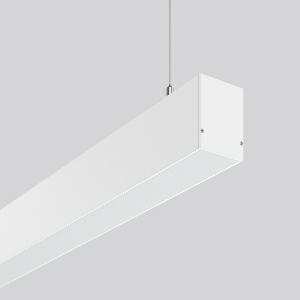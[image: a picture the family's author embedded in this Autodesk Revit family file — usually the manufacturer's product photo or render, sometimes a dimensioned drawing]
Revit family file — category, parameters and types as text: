
# Revit family: less_is_more_50_312317_002_1_9efc
name_source: partatom
category: Lighting Fixtures
units: mm (PartAtom-declared; Revit-internal decimal feet)

## family parameters
Cut with Voids When Loaded = No
Host = Face
Light Source = No
Part Type = Normal
Room Calculation Point = No
Round Connector Dimension = Use Diameter
Shared = No

## types (1)
- LESS IS MORE 50 (1 x LED Modul 840, 4000 lm, 4000)
    Apparent Load = 34 VA
    CIE Flux Codes = 49 80 96 63 100
    Color Rendering = 80
    Color Temperature = 4000
    Default Elevation = 1800 mm
    Description = Series: LESS IS MORE 50
Linear pendant luminaire for aesthetically sophisticated lighting. Housing: extruded aluminium profile, powder-coated. End cap aluminium powder-coated. Canopy made of aluminium, powder-coated. Diffuser made of non-yellowing plastic (PMMA), opal. Direct 65%, indirect 35% light emission. Suitable for pendant. 2-point steel cable suspension freely positionable and infinitely height-adjustable. Special lengths available on request. LED unit with integrated converter interchangeable and removable. Suitable for through-wiring. With sensors or as a safety luminaire on request. 
Colour: traffic white, matt (RAL 9016)
Length: 847 mm
Width: 57 mm
Height: 75 mm
Suspension length: 2000 mm
Lamp: LED
Socket: without socket
Colour temperature: 4000K
Colour rendering index (CRI): 80
Light source: LED
Socket lamp2: Without base
Colour temperature: 4000K
System power: 34 W
Rated luminous flux: 4000 lm
Luminous efficiency: 118 lm/W
Control gear: Regulated power supply
Control gear: Regulated power supply
Protection class: I
Type of protection: IP 20
    Height = 75 mm
    Lamp = 1 x LED Modul 840
    Lamp Light Flux = 4000 lm
    Lamp count = 1
    Length = 847 mm
    Lifetime = 50000 h
    Luminous efficacy = 118 lm/W
    Manufacturer = RZB
    ModVariant = No
    Model = 312317.002.1
    Mounting Place = Ceiling
    Mounting Type = Pendant
    Number of Poles = 1
    OnlyDefault = Yes
    Power Factor = 1
    Product Name = LESS IS MORE 50
    Product group = Pendant LED linear luminaires
    ProductGroupID = 907
    Protection Class = Protection class I
    Protection Degree = IP 20
    RLX_Detail_Level = 1
    RLX_Emergency_Light_Flux = 0 lm
    RLX_Emergency_Type = 0
    RLX_Emergency_Type_DB = No
    RlxData = <blob elided: 31625 chars, md5=90b03f43>
    Socket = socket
    Standby Power = 0 W
    System Light Flux = 4000 lm
    System Power = 34 W
    Type Comments = Product without accessories
    Type Image = 312318.002.jpg
    URL = http://relux.com
    VarID = ---
    Voltage = 230 V
    Voltage Range = 220-240 V
    Weight = 0.00 kg
    Width = 57 mm

## geometry (parser evidence)
native form markers: Blend x4, Sweep x13
no freeform markers — native parametric forms only
